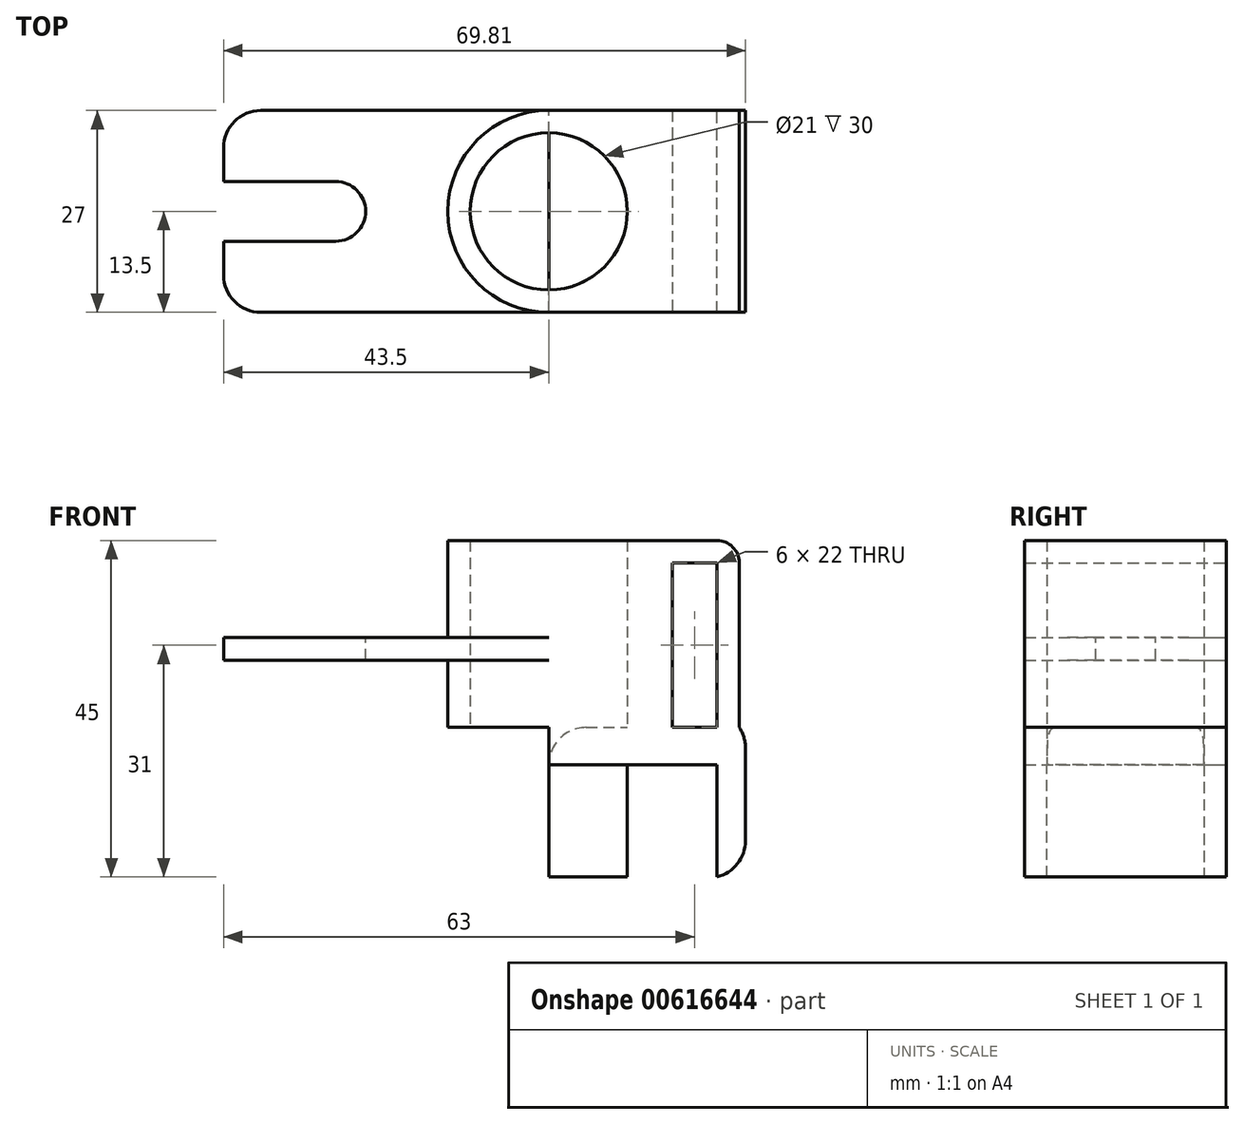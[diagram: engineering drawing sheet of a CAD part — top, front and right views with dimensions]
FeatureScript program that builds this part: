
annotation { "Feature Type Name" : "Feature", "Feature Type Description" : "" }
export const myFeature = defineFeature(function(context is Context, id is Id, definition is map)
    precondition{}
    {
        {
            var Q0;
            Q0=qCreatedBy(makeId("Top.planeOp"),FACE);
            var sketch = newSketch(context, id + "F0", { "sketchPlane" : qUnion([Q0])});
            skCircle(sketch, "E0", {"center": v(0, 0) * mm, "radius": 10.5 * mm});
            skCircle(sketch, "E1", {"center": v(0, 0) * mm, "radius": 13.5 * mm});
            skLineSegment(sketch, "E2", {"start": v(0, 13.5) * mm, "end": v(25.5, 13.5) * mm});
            skLineSegment(sketch, "E3", {"start": v(25.5, 13.5) * mm, "end": v(25.5, -13.5) * mm});
            skLineSegment(sketch, "E4", {"start": v(0, -13.5) * mm, "end": v(25.5, -13.5) * mm});
            skLineSegment(sketch, "E5", {"start": v(13.5, 0) * mm, "end": v(13.5, 13.5) * mm});
            skLineSegment(sketch, "E6", {"start": v(13.5, 0) * mm, "end": v(13.5, -13.5) * mm});
            skLineSegment(sketch, "E7", {"start": v(16.5, 13.5) * mm, "end": v(16.5, -13.5) * mm, "construction": true});
            skLineSegment(sketch, "E8", {"start": v(22.5, 13.5) * mm, "end": v(22.5, -13.5) * mm, "construction": true});
            skLineSegment(sketch, "E9", {"start": v(16.5, 13.5) * mm, "end": v(16.5, -13.5) * mm});
            skLineSegment(sketch, "E10", {"start": v(22.5, -13.5) * mm, "end": v(22.5, 13.5) * mm});
            skSolve(sketch);
        }
        {
            var Q0;
            Q0=qSketchRegion(id+"F0",true);
            extrude(context, id + "F1", {"entities" : qUnion([Q0]), "depth" : 3 * mm});
        }
        {
            var Q0;
            Q0=makeQuery(id+"F0.imprint","IMPRINT",FACE,{"disambiguationData":[TD([[makeQuery(id+"F0.imprint","IMPRINT",EDGE,{"derivedFrom":sQuery(id+"F0.wireOp",EDGE,"E0")}),-1.0]])]});
            var Q1;
            {var subQ3=sQuery(id+"F0.wireOp",EDGE,"E5");Q1=makeQuery(id+"F0.imprint","IMPRINT",FACE,{"disambiguationData":[TD([[makeQuery(id+"F0.imprint","IMPRINT",EDGE,{"derivedFrom":subQ3}),1.0]])]});}
            var Q2;
            {var subQ1=sQuery(id+"F0.wireOp",EDGE,"E5");Q2=makeQuery(id+"F0.imprint","IMPRINT",FACE,{"disambiguationData":[TD([[makeQuery(id+"F0.imprint","IMPRINT",EDGE,{"derivedFrom":subQ1}),-1.0]])]});}
            var Q3;
            {var subQ0=sQuery(id+"F0.wireOp",EDGE,"E3");Q3=makeQuery(id+"F0.imprint","IMPRINT",FACE,{"disambiguationData":[TD([[makeQuery(id+"F0.imprint","IMPRINT",EDGE,{"derivedFrom":subQ0}),-1.0]])]});}
            var Q4;
            {var subQ3=sQuery(id+"F0.wireOp",EDGE,"E6");Q4=makeQuery(id+"F0.imprint","IMPRINT",FACE,{"disambiguationData":[TD([[makeQuery(id+"F0.imprint","IMPRINT",EDGE,{"derivedFrom":subQ3}),-1.0]])]});}
            extrude(context, id + "F2", {"entities" : qUnion([Q0, Q1, Q2, Q3, Q4]), "operationType" : NewBodyOperationType.ADD, "oppositeDirection" : true, "depth" : 22 * mm});
        }
        {
            var Q0;
            Q0=makeQuery(id+"F2.opExtrude","CAP_EDGE",EDGE,{"disambiguationData":[OSD([sQuery(id+"F0.wireOp",EDGE,"E9")])],"isStart":true});
            var Q1;
            Q1=makeQuery(id+"F2.opExtrude","CAP_EDGE",EDGE,{"disambiguationData":[OSD([sQuery(id+"F0.wireOp",EDGE,"E10")])],"isStart":true});
            var Q2;
            Q2=makeQuery(id+"F1.opExtrude","CAP_EDGE",EDGE,{"disambiguationData":[OSD([sQuery(id+"F0.wireOp",EDGE,"E3")])],"isStart":false});
            fillet(context, id + "F3", {"entities" : qUnion([Q0, Q1, Q2]), "radius" : 3 * mm, "tangentPropagation" : true, "allowEdgeOverflow" : false});
        }
        {
            var Q0;
            Q0=makeQuery(id+"F2.opExtrude","CAP_FACE",FACE,{"disambiguationData":[OSD([sQuery(id+"F0.wireOp",EDGE,"E0"),sQuery(id+"F0.wireOp",EDGE,"E1"),sQuery(id+"F0.wireOp",EDGE,"E2"),sQuery(id+"F0.wireOp",EDGE,"E4"),sQuery(id+"F0.wireOp",EDGE,"E9")])],"isStart":false});
            cPlane(context, id + "F4", {"entities" : qUnion([Q0]), "cplaneType" : CPlaneType.OFFSET, "offset" : 12 * mm, "oppositeDirection" : true, "width" : 150 * mm, "height" : 150 * mm});
        }
        {
            var Q0;
            Q0=qCreatedBy(id+"F4.planeOp",FACE);
            var sketch = newSketch(context, id + "F5", { "sketchPlane" : qUnion([Q0])});
            skCircle(sketch, "E11.0", {"center": v(0, 0) * mm, "radius": 10.5 * mm});
            skArc(sketch, "E12.0.0", {"start": v(0, 13.5) * mm, "mid": v(-13.5, 0) * mm, "end": v(0, -13.5) * mm});
            skLineSegment(sketch, "E12.0.1", {"start": v(0, -13.5) * mm, "end": v(16.5, -13.5) * mm});
            skLineSegment(sketch, "E12.0.2", {"start": v(16.5, -13.5) * mm, "end": v(16.5, 13.5) * mm});
            skLineSegment(sketch, "E12.0.3", {"start": v(16.5, 13.5) * mm, "end": v(0, 13.5) * mm});
            skLineSegment(sketch, "E13", {"start": v(0, -13.5) * mm, "end": v(-43.5, -13.5) * mm});
            skLineSegment(sketch, "E14", {"start": v(-43.5, -13.5) * mm, "end": v(-43.5, -4) * mm});
            skLineSegment(sketch, "E15", {"start": v(-43.5, 13.5) * mm, "end": v(0, 13.5) * mm});
            skLineSegment(sketch, "E16.bottom", {"start": v(0, 0) * mm, "end": v(-28.5, 0) * mm, "construction": true});
            skLineSegment(sketch, "E16.top", {"start": v(0, 4) * mm, "end": v(-43.5, 4) * mm, "construction": true});
            skLineSegment(sketch, "E16.left", {"start": v(0, 0) * mm, "end": v(0, 4) * mm, "construction": true});
            skLineSegment(sketch, "E17.MirrorCS", {"start": v(0, -4) * mm, "end": v(-43.5, -4) * mm, "construction": true});
            skLineSegment(sketch, "E18", {"start": v(-43.5, 0) * mm, "end": v(-13.5, 0) * mm, "construction": true});
            skPoint(sketch, "E19", {"position": v(-28.5, 0) * mm});
            skArc(sketch, "E20", {"start": v(-28.5, -4) * mm, "mid": v(-24.5, 0) * mm, "end": v(-28.5, 4) * mm});
            skLineSegment(sketch, "E21", {"start": v(-28.5, 4) * mm, "end": v(-43.5, 4) * mm});
            skLineSegment(sketch, "E22", {"start": v(-43.5, -4) * mm, "end": v(-28.5, -4) * mm});
            skLineSegment(sketch, "E23.trimOffspring", {"start": v(-43.5, 4) * mm, "end": v(-43.5, 13.5) * mm});
            skSolve(sketch);
        }
        {
            var Q0;
            Q0=makeQuery(id+"F5.imprint","IMPRINT",FACE,{"disambiguationData":[TD([[makeQuery(id+"F5.imprint","IMPRINT",EDGE,{"derivedFrom":sQuery(id+"F5.wireOp",EDGE,"E11.0")}),-1.0]])]});
            extrude(context, id + "F6", {"entities" : qUnion([Q0]), "oppositeDirection" : true, "depth" : 12 * mm});
        }
        {
            var Q0;
            Q0=qSketchRegion(id+"F5",true);
            extrude(context, id + "F7", {"entities" : qUnion([Q0]), "operationType" : NewBodyOperationType.ADD, "depth" : 3 * mm});
        }
        {
            var Q0;
            Q0=makeQuery(id+"F7.opExtrude","SWEPT_EDGE",EDGE,{"disambiguationData":[OSD([sQuery(id+"F5.wireOp",EDGE,"E15"),sQuery(id+"F5.wireOp",EDGE,"E23.trimOffspring")])]});
            var Q1;
            Q1=makeQuery(id+"F7.opExtrude","SWEPT_EDGE",EDGE,{"disambiguationData":[OSD([sQuery(id+"F5.wireOp",EDGE,"E13"),sQuery(id+"F5.wireOp",EDGE,"E14")])]});
            fillet(context, id + "F8", {"entities" : qUnion([Q0, Q1]), "radius" : 5 * mm, "tangentPropagation" : true, "allowEdgeOverflow" : false});
        }
        {
            var Q0;
            Q0=makeQuery(id+"F2.opExtrude","CAP_FACE",FACE,{"disambiguationData":[OSD([sQuery(id+"F0.wireOp",EDGE,"E0"),sQuery(id+"F0.wireOp",EDGE,"E1"),sQuery(id+"F0.wireOp",EDGE,"E2"),sQuery(id+"F0.wireOp",EDGE,"E4"),sQuery(id+"F0.wireOp",EDGE,"E9")])],"isStart":false});
            var sketch = newSketch(context, id + "F9", { "sketchPlane" : qUnion([Q0])});
            skArc(sketch, "E24.0", {"start": v(0, -10.5) * mm, "mid": v(10.5, 0) * mm, "end": v(0, 10.5) * mm, "construction": true});
            skLineSegment(sketch, "E25.0", {"start": v(22.5, 13.5) * mm, "end": v(22.5, -13.5) * mm, "construction": true});
            skLineSegment(sketch, "E26.0", {"start": v(16.5, -13.5) * mm, "end": v(16.5, 13.5) * mm, "construction": true});
            skLineSegment(sketch, "E27", {"start": v(0, 10.5) * mm, "end": v(0, -10.5) * mm});
            skArc(sketch, "E28", {"start": v(0, -10.5) * mm, "mid": v(10.52, 0) * mm, "end": v(0, 10.5) * mm});
            skLineSegment(sketch, "E29", {"start": v(26.3, 13.5) * mm, "end": v(26.3, -13.5) * mm});
            skLineSegment(sketch, "E30", {"start": v(26.3, -13.5) * mm, "end": v(0, -13.5) * mm});
            skLineSegment(sketch, "E31", {"start": v(0, -13.5) * mm, "end": v(0, -10.5) * mm});
            skLineSegment(sketch, "E32", {"start": v(0, 10.5) * mm, "end": v(0, 13.5) * mm});
            skLineSegment(sketch, "E33", {"start": v(0, 13.5) * mm, "end": v(26.3, 13.5) * mm});
            skLineSegment(sketch, "E34", {"start": v(22.5, 13.5) * mm, "end": v(22.5, -13.5) * mm});
            skLineSegment(sketch, "E35", {"start": v(0, 10.5) * mm, "end": v(26.3, 10.5) * mm});
            skLineSegment(sketch, "E36", {"start": v(0, -10.5) * mm, "end": v(26.3, -10.5) * mm});
            skSolve(sketch);
        }
        {
            var Q0;
            {var subQ0=sQuery(id+"F9.wireOp",EDGE,"E27");Q0=makeQuery(id+"F9.imprint","IMPRINT",FACE,{"disambiguationData":[TD([[makeQuery(id+"F9.imprint","IMPRINT",EDGE,{"derivedFrom":subQ0}),1.0]])]});}
            var Q1;
            {var subQ0=sQuery(id+"F9.wireOp",EDGE,"E29");Q1=makeQuery(id+"F9.imprint","IMPRINT",FACE,{"disambiguationData":[TD([[makeQuery(id+"F9.imprint","IMPRINT",EDGE,{"derivedFrom":subQ0}),-1.0]])]});}
            extrude(context, id + "F10", {"entities" : qUnion([Q0, Q1]), "depth" : 20 * mm, "offsetDistance" : 25 * mm});
        }
        {
            var Q0;
            Q0 = qSketchRegion(id + "F9", true);
            var Q1;
            {var subQ0=sQuery(id+"F9.wireOp",EDGE,"E36");var subQ1=sQuery(id+"F9.wireOp",EDGE,"E28");var subQ2=makeQuery(id+"F9.imprint","INTERSECT",VERTEX,{"derivedFrom":[subQ1,subQ0]});Q1=makeQuery(id+"F9.imprint","IMPRINT",FACE,{"disambiguationData":[TD([[makeQuery(id+"F9.imprint","IMPRINT",EDGE,{"disambiguationData":[TD([[subQ2,-1.0]])],"derivedFrom":subQ1}),-1.0]])]});}
            var Q2;
            {var subQ0=sQuery(id+"F9.wireOp",EDGE,"E35");var subQ1=sQuery(id+"F9.wireOp",EDGE,"E34");var subQ2=makeQuery(id+"F9.imprint","INTERSECT",VERTEX,{"derivedFrom":[subQ1,subQ0]});Q2=makeQuery(id+"F9.imprint","IMPRINT",FACE,{"disambiguationData":[TD([[makeQuery(id+"F9.imprint","IMPRINT",EDGE,{"disambiguationData":[TD([[subQ2,-1.0]])],"derivedFrom":subQ1}),-1.0]])]});}
            extrude(context, id + "F11", {"entities" : qUnion([Q0, Q1, Q2]), "operationType" : NewBodyOperationType.ADD, "depth" : 5 * mm, "offsetDistance" : 25 * mm});
        }
        {
            var Q0;
            {var subQ0=sQuery(id+"F9.wireOp",EDGE,"E27");Q0=makeQuery(id+"F11.boolean.opBoolean","MERGE",EDGE,{"derivedFrom":[makeQuery(id+"F10.opExtrude","CAP_EDGE",EDGE,{"disambiguationData":[OSD([subQ0])],"isStart":true}),makeQuery(id+"F11.opExtrude","CAP_EDGE",EDGE,{"disambiguationData":[OSD([subQ0,sQuery(id+"F9.wireOp",EDGE,"E31"),sQuery(id+"F9.wireOp",EDGE,"E32")])],"isStart":true})]});}
            var Q1;
            Q1=makeQuery(id+"F10.opExtrude","CAP_EDGE",EDGE,{"disambiguationData":[OSD([sQuery(id+"F9.wireOp",EDGE,"E29")])],"isStart":true});
            var Q2;
            Q2=makeQuery(id+"F10.opExtrude","CAP_EDGE",EDGE,{"disambiguationData":[OSD([sQuery(id+"F9.wireOp",EDGE,"E29")])],"isStart":false});
            fillet(context, id + "F12", {"entities" : qUnion([Q0, Q1, Q2]), "radius" : 5 * mm, "tangentPropagation" : true, "allowEdgeOverflow" : false});
        }
    });
